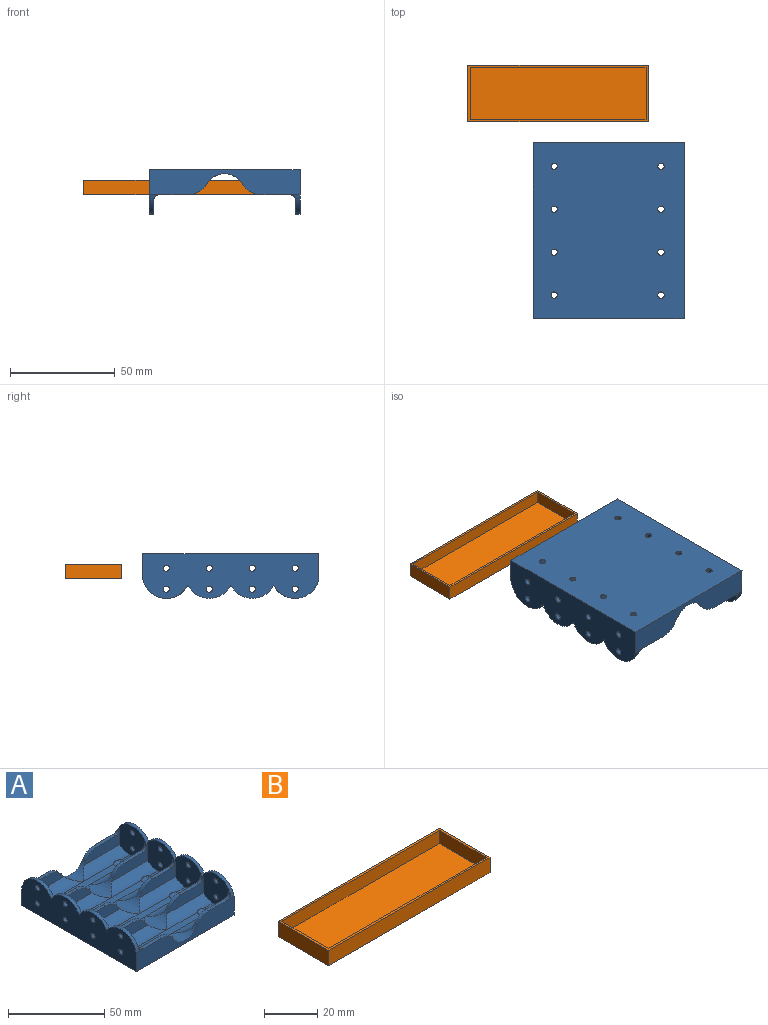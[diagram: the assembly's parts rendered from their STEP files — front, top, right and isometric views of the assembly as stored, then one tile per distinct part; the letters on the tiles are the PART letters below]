
ASSEMBLY  parts=2 mates=1
PART A: 158 faces, bbox 72x84x21.4 mm
  f0: plane 84x21.43mm, normal (-1,0,0), area 1579.3mm2, adj f1,f144,f145,f146,f147,f148,f149,f150
  f1: cylinder r=1.5mm len=3mm, axis (-1,0,0), area 18.8mm2, adj f0,f2
  f2: plane 82.05x19.43mm, normal (1,0,0), area 1230.6mm2, adj f1,f3,f120,f121,f122,f123,f124,f125
  f3: cylinder r=3mm len=3mm, axis (0,-1,0), area 7.1mm2, adj f2,f4,f120,f152
  f4: plane 13.68x2mm, normal (0,0,1), area 27.4mm2, adj f3,f5,f120,f151
  f5: cylinder r=10mm len=8.66mm, axis (0,-1,0), area 20.9mm2, adj f4,f6,f120,f151
  f6: cylinder r=10mm len=17.32mm, axis (0,-1,0), area 98.7mm2, adj f5,f7,f118,f119,f120,f121,f151
  f7: cylinder r=10mm len=34mm, axis (-1,0,0), area 237.5mm2, adj f6,f8,f114,f116,f117,f118
  f8: plane 45.41x4.22mm, normal (0,0,1), area 187.5mm2, adj f7,f9,f15,f19,f121,f123
  f9: cone r=1.5mm half-angle=45deg, axis (0,0,1), area 9.1mm2, adj f8,f10,f13,f157
  f10: bspline ~5.59x2.36mm, area 12.3mm2, adj f9,f11,f12,f123
  f11: cylinder r=1.5mm len=2.39mm, axis (0,0,1), area 0mm2, adj f10,f157
  f12: cone r=1.5mm half-angle=45deg, axis (0,0,1), area 9.1mm2, adj f10,f13,f122,f157
  f13: bspline ~5.59x2.36mm, area 12.3mm2, adj f9,f12,f14,f121
  f14: cylinder r=1.5mm len=2.39mm, axis (0,0,1), area 0mm2, adj f13,f157
  f15: cone r=1.5mm half-angle=45deg, axis (0,0,1), area 9.1mm2, adj f8,f16,f114,f157
  f16: bspline ~5.59x2.36mm, area 12.3mm2, adj f15,f17,f18,f19
  f17: cylinder r=1.5mm len=2.39mm, axis (0,0,1), area 0mm2, adj f16,f157
  f18: cone r=1.5mm half-angle=45deg, axis (0,0,1), area 9.1mm2, adj f16,f114,f116,f157
  f19: cylinder r=10mm len=34mm, axis (-1,0,0), area 237.5mm2, adj f8,f16,f20,f113,f116,f117
  f20: cylinder r=10mm len=17.32mm, axis (0,-1,0), area 155.5mm2, adj f19,f21,f23,f109,f112,f113,f123,f124
  f21: cylinder r=10mm len=8.66mm, axis (0,-1,0), area 20.9mm2, adj f20,f22,f124,f126
  f22: plane 13.68x2mm, normal (0,0,1), area 27.4mm2, adj f21,f124,f125,f126
  f23: cylinder r=10mm len=34mm, axis (-1,0,0), area 237.5mm2, adj f20,f24,f106,f108,f109,f117
  f24: plane 45.41x4.22mm, normal (0,0,1), area 187.5mm2, adj f23,f25,f29,f100,f127,f129
  f25: cone r=1.5mm half-angle=45deg, axis (0,0,1), area 9.1mm2, adj f24,f26,f106,f157
  f26: bspline ~5.59x2.36mm, area 12.3mm2, adj f25,f27,f28,f29
  f27: cone r=1.5mm half-angle=45deg, axis (0,0,1), area 9.1mm2, adj f26,f106,f108,f157
  f28: cylinder r=1.5mm len=2.39mm, axis (0,0,1), area 0mm2, adj f26,f157
  f29: cylinder r=10mm len=34mm, axis (-1,0,0), area 237.5mm2, adj f24,f26,f30,f97,f108,f117
  f30: plane 26.86x10mm, normal (0,1,0), area 168.1mm2, adj f29,f31,f95,f96,f97,f117
  f31: cylinder r=10mm len=8.66mm, axis (0,1,0), area 20.9mm2, adj f30,f32,f96,f97
  f32: plane 26.86x10mm, normal (0,-1,0), area 168.1mm2, adj f31,f33,f95,f96,f97,f117
  f33: cylinder r=10mm len=34mm, axis (-1,0,0), area 237.5mm2, adj f32,f34,f92,f94,f97,f117
  f34: plane 45.41x4.22mm, normal (0,0,1), area 187.5mm2, adj f33,f35,f41,f45,f133,f135
  f35: cone r=1.5mm half-angle=45deg, axis (0,0,1), area 9.1mm2, adj f34,f36,f39,f157
  f36: bspline ~5.59x2.36mm, area 12.3mm2, adj f35,f37,f38,f135
  f37: cylinder r=1.5mm len=2.39mm, axis (0,0,1), area 0mm2, adj f36,f157
  f38: cone r=1.5mm half-angle=45deg, axis (0,0,1), area 9.1mm2, adj f36,f39,f134,f157
  f39: bspline ~5.59x2.36mm, area 12.3mm2, adj f35,f38,f40,f133
  f40: cylinder r=1.5mm len=2.39mm, axis (0,0,1), area 0mm2, adj f39,f157
  f41: cone r=1.5mm half-angle=45deg, axis (0,0,1), area 9.1mm2, adj f34,f42,f92,f157
  f42: bspline ~5.59x2.36mm, area 12.3mm2, adj f41,f43,f44,f45
  f43: cylinder r=1.5mm len=2.39mm, axis (0,0,1), area 0mm2, adj f42,f157
  f44: cone r=1.5mm half-angle=45deg, axis (0,0,1), area 9.1mm2, adj f42,f92,f94,f157
  f45: cylinder r=10mm len=34mm, axis (-1,0,0), area 237.5mm2, adj f34,f42,f46,f91,f94,f117
  f46: cylinder r=10mm len=17.32mm, axis (0,1,0), area 155.5mm2, adj f45,f47,f49,f87,f90,f91,f135,f136
  f47: cylinder r=10mm len=8.66mm, axis (0,1,0), area 20.9mm2, adj f46,f48,f136,f138
  f48: plane 13.68x2mm, normal (0,0,1), area 27.4mm2, adj f47,f136,f137,f138
  f49: cylinder r=10mm len=34mm, axis (-1,0,0), area 237.5mm2, adj f46,f50,f84,f86,f87,f117
  f50: plane 45.41x4.22mm, normal (0,0,1), area 187.5mm2, adj f49,f51,f55,f78,f139,f141
  f51: cone r=1.5mm half-angle=45deg, axis (0,0,1), area 9.1mm2, adj f50,f52,f84,f157
  f52: bspline ~5.59x2.36mm, area 12.3mm2, adj f51,f53,f54,f55
  f53: cone r=1.5mm half-angle=45deg, axis (0,0,1), area 9.1mm2, adj f52,f84,f86,f157
  f54: cylinder r=1.5mm len=2.39mm, axis (0,0,1), area 0mm2, adj f52,f157
  f55: cylinder r=10mm len=34mm, axis (-1,0,0), area 237.5mm2, adj f50,f52,f56,f75,f86,f117
  f56: plane 26.86x10mm, normal (0,1,0), area 168.1mm2, adj f55,f57,f73,f74,f75,f117
  f57: cylinder r=3mm len=3mm, axis (0,-1,0), area 7.1mm2, adj f56,f58,f73,f117
  f58: cylinder r=11.43mm len=21.5mm, axis (1,0,0), area 62.1mm2, adj f57,f59,f72,f117,f156
  f59: plane 84x21.43mm, normal (1,0,0), area 1579.3mm2, adj f58,f60,f61,f62,f63,f64,f65,f66
  f60: cylinder r=1.5mm len=3mm, axis (-1,0,0), area 18.8mm2, adj f59,f117
  f61: cylinder r=1.5mm len=3mm, axis (-1,0,0), area 18.8mm2, adj f59,f117
  f62: cylinder r=1.5mm len=3mm, axis (-1,0,0), area 18.8mm2, adj f59,f117
  f63: cylinder r=1.5mm len=3mm, axis (-1,0,0), area 18.8mm2, adj f59,f117
  f64: cylinder r=1.5mm len=3mm, axis (-1,0,0), area 18.8mm2, adj f59,f117
  f65: cylinder r=1.5mm len=3mm, axis (-1,0,0), area 18.8mm2, adj f59,f117
  f66: cylinder r=1.5mm len=3mm, axis (-1,0,0), area 18.8mm2, adj f59,f117
  f67: cylinder r=1.5mm len=3mm, axis (-1,0,0), area 18.8mm2, adj f59,f117
  f68: cylinder r=11.43mm len=20.5mm, axis (1,0,0), area 50.9mm2, adj f59,f69,f72,f117
  f69: cylinder r=11.43mm len=21.5mm, axis (1,0,0), area 62.1mm2, adj f59,f68,f70,f117,f151
  f70: cylinder r=3mm len=3mm, axis (0,1,0), area 7.1mm2, adj f69,f71,f117,f118
  f71: plane 13.68x2mm, normal (0,0,1), area 27.4mm2, adj f70,f118,f119,f151
  f72: cylinder r=11.43mm len=20.5mm, axis (1,0,0), area 50.9mm2, adj f58,f59,f68,f117
  f73: plane 13.68x2mm, normal (0,0,1), area 27.4mm2, adj f56,f57,f74,f156
  f74: cylinder r=10mm len=8.66mm, axis (0,1,0), area 20.9mm2, adj f56,f73,f75,f156
  f75: cylinder r=10mm len=17.32mm, axis (0,1,0), area 98.7mm2, adj f55,f56,f74,f76,f141,f142,f156
  f76: cylinder r=10mm len=8.66mm, axis (0,1,0), area 20.9mm2, adj f75,f77,f142,f156
  f77: plane 13.68x2mm, normal (0,0,1), area 27.4mm2, adj f76,f142,f143,f156
  f78: cone r=1.5mm half-angle=45deg, axis (0,0,1), area 9.1mm2, adj f50,f79,f82,f157
  f79: bspline ~5.59x2.36mm, area 12.3mm2, adj f78,f80,f81,f139
  f80: cone r=1.5mm half-angle=45deg, axis (0,0,1), area 9.1mm2, adj f79,f82,f140,f157
  f81: cylinder r=1.5mm len=2.39mm, axis (0,0,1), area 0mm2, adj f79,f157
  f82: bspline ~5.59x2.36mm, area 12.3mm2, adj f78,f80,f83,f141
  f83: cylinder r=1.5mm len=2.39mm, axis (0,0,1), area 0mm2, adj f82,f157
  f84: bspline ~5.59x2.36mm, area 12.3mm2, adj f49,f51,f53,f85
  f85: cylinder r=1.5mm len=2.39mm, axis (0,0,1), area 0mm2, adj f84,f157
  f86: plane 6.21x4.22mm, normal (0,0,1), area 24.1mm2, adj f49,f53,f55,f117
  f87: plane 26.86x10mm, normal (0,-1,0), area 168.1mm2, adj f46,f49,f88,f89,f90,f117
  f88: cylinder r=3mm len=3mm, axis (0,-1,0), area 9.4mm2, adj f87,f89,f91,f117
  f89: plane 13.68x2mm, normal (0,0,1), area 27.4mm2, adj f87,f88,f90,f91
  f90: cylinder r=10mm len=8.66mm, axis (0,1,0), area 20.9mm2, adj f46,f87,f89,f91
  f91: plane 26.86x10mm, normal (0,1,0), area 168.1mm2, adj f45,f46,f88,f89,f90,f117
  f92: bspline ~5.59x2.36mm, area 12.3mm2, adj f33,f41,f44,f93
  f93: cylinder r=1.5mm len=2.39mm, axis (0,0,1), area 0mm2, adj f92,f157
  f94: plane 6.21x4.22mm, normal (0,0,1), area 24.1mm2, adj f33,f44,f45,f117
  f95: cylinder r=3mm len=3mm, axis (0,-1,0), area 9.4mm2, adj f30,f32,f96,f117
  f96: plane 13.68x2mm, normal (0,0,1), area 27.4mm2, adj f30,f31,f32,f95
  f97: cylinder r=10mm len=17.32mm, axis (0,1,0), area 155.5mm2, adj f29,f30,f31,f32,f33,f98,f129,f130
  f98: cylinder r=10mm len=8.66mm, axis (0,1,0), area 20.9mm2, adj f97,f99,f130,f132
  f99: plane 13.68x2mm, normal (0,0,1), area 27.4mm2, adj f98,f130,f131,f132
  f100: cone r=1.5mm half-angle=45deg, axis (0,0,1), area 9.1mm2, adj f24,f101,f104,f157
  f101: bspline ~5.59x2.36mm, area 12.3mm2, adj f100,f102,f103,f127
  f102: cone r=1.5mm half-angle=45deg, axis (0,0,1), area 9.1mm2, adj f101,f104,f128,f157
  f103: cylinder r=1.5mm len=2.39mm, axis (0,0,1), area 0mm2, adj f101,f157
  f104: bspline ~5.59x2.36mm, area 12.3mm2, adj f100,f102,f105,f129
  f105: cylinder r=1.5mm len=2.39mm, axis (0,0,1), area 0mm2, adj f104,f157
  f106: bspline ~5.59x2.36mm, area 12.3mm2, adj f23,f25,f27,f107
  f107: cylinder r=1.5mm len=2.39mm, axis (0,0,1), area 0mm2, adj f106,f157
  f108: plane 6.21x4.22mm, normal (0,0,1), area 24.1mm2, adj f23,f27,f29,f117
  f109: plane 26.86x10mm, normal (0,-1,0), area 168.1mm2, adj f20,f23,f110,f111,f112,f117
  f110: plane 13.68x2mm, normal (0,0,1), area 27.4mm2, adj f109,f111,f112,f113
  f111: cylinder r=3mm len=3mm, axis (0,1,0), area 9.4mm2, adj f109,f110,f113,f117
  f112: cylinder r=10mm len=8.66mm, axis (0,-1,0), area 20.9mm2, adj f20,f109,f110,f113
  f113: plane 26.86x10mm, normal (0,1,0), area 168.1mm2, adj f19,f20,f110,f111,f112,f117
  f114: bspline ~5.59x2.36mm, area 12.3mm2, adj f7,f15,f18,f115
  f115: cylinder r=1.5mm len=2.39mm, axis (0,0,1), area 0mm2, adj f114,f157
  f116: plane 6.21x4.22mm, normal (0,0,1), area 24.1mm2, adj f7,f18,f19,f117
  f117: plane 82.05x19.43mm, normal (-1,0,0), area 1230.6mm2, adj f7,f19,f23,f29,f30,f32,f33,f45
  f118: plane 26.86x10mm, normal (0,-1,0), area 168.1mm2, adj f6,f7,f70,f71,f117,f119
  f119: cylinder r=10mm len=8.66mm, axis (0,-1,0), area 20.9mm2, adj f6,f71,f118,f151
  f120: plane 26.86x10mm, normal (0,-1,0), area 168.1mm2, adj f2,f3,f4,f5,f6,f121
  f121: cylinder r=10mm len=34mm, axis (-1,0,0), area 237.5mm2, adj f2,f6,f8,f13,f120,f122
  f122: plane 5.21x4.22mm, normal (0,0,1), area 19.9mm2, adj f2,f12,f121,f123
  f123: cylinder r=10mm len=34mm, axis (-1,0,0), area 237.5mm2, adj f2,f8,f10,f20,f122,f124
  f124: plane 26.86x10mm, normal (0,1,0), area 168.1mm2, adj f2,f20,f21,f22,f123,f125
  f125: cylinder r=3mm len=3mm, axis (0,-1,0), area 9.4mm2, adj f2,f22,f124,f126
  f126: plane 26.86x10mm, normal (0,-1,0), area 168.1mm2, adj f2,f20,f21,f22,f125,f127
  f127: cylinder r=10mm len=34mm, axis (-1,0,0), area 237.5mm2, adj f2,f20,f24,f101,f126,f128
  f128: plane 5.21x4.22mm, normal (0,0,1), area 19.9mm2, adj f2,f102,f127,f129
  f129: cylinder r=10mm len=34mm, axis (-1,0,0), area 237.5mm2, adj f2,f24,f97,f104,f128,f130
  f130: plane 26.86x10mm, normal (0,1,0), area 168.1mm2, adj f2,f97,f98,f99,f129,f131
  f131: cylinder r=3mm len=3mm, axis (0,1,0), area 9.4mm2, adj f2,f99,f130,f132
  f132: plane 26.86x10mm, normal (0,-1,0), area 168.1mm2, adj f2,f97,f98,f99,f131,f133
  f133: cylinder r=10mm len=34mm, axis (-1,0,0), area 237.5mm2, adj f2,f34,f39,f97,f132,f134
  f134: plane 5.21x4.22mm, normal (0,0,1), area 19.9mm2, adj f2,f38,f133,f135
  f135: cylinder r=10mm len=34mm, axis (-1,0,0), area 237.5mm2, adj f2,f34,f36,f46,f134,f136
  f136: plane 26.86x10mm, normal (0,1,0), area 168.1mm2, adj f2,f46,f47,f48,f135,f137
  f137: cylinder r=3mm len=3mm, axis (0,1,0), area 9.4mm2, adj f2,f48,f136,f138
  f138: plane 26.86x10mm, normal (0,-1,0), area 168.1mm2, adj f2,f46,f47,f48,f137,f139
  f139: cylinder r=10mm len=34mm, axis (-1,0,0), area 237.5mm2, adj f2,f46,f50,f79,f138,f140
  f140: plane 5.21x4.22mm, normal (0,0,1), area 19.9mm2, adj f2,f80,f139,f141
  f141: cylinder r=10mm len=34mm, axis (-1,0,0), area 237.5mm2, adj f2,f50,f75,f82,f140,f142
  f142: plane 26.86x10mm, normal (0,1,0), area 168.1mm2, adj f2,f75,f76,f77,f141,f143
  f143: cylinder r=3mm len=3mm, axis (0,1,0), area 7.1mm2, adj f2,f77,f142,f155
  f144: cylinder r=1.5mm len=3mm, axis (-1,0,0), area 18.8mm2, adj f0,f2
  f145: cylinder r=1.5mm len=3mm, axis (-1,0,0), area 18.8mm2, adj f0,f2
  f146: cylinder r=1.5mm len=3mm, axis (-1,0,0), area 18.8mm2, adj f0,f2
  f147: cylinder r=1.5mm len=3mm, axis (-1,0,0), area 18.8mm2, adj f0,f2
  f148: cylinder r=1.5mm len=3mm, axis (-1,0,0), area 18.8mm2, adj f0,f2
  f149: cylinder r=1.5mm len=3mm, axis (-1,0,0), area 18.8mm2, adj f0,f2
  f150: cylinder r=1.5mm len=3mm, axis (-1,0,0), area 18.8mm2, adj f0,f2
  f151: plane 72x12mm, normal (0,1,0), area 690.8mm2, adj f0,f4,f5,f6,f59,f69,f71,f119
  f152: cylinder r=11.43mm len=21.5mm, axis (1,0,0), area 62.1mm2, adj f0,f2,f3,f151,f153
  f153: cylinder r=11.43mm len=20.5mm, axis (1,0,0), area 50.9mm2, adj f0,f2,f152,f154
  f154: cylinder r=11.43mm len=20.5mm, axis (1,0,0), area 50.9mm2, adj f0,f2,f153,f155
  f155: cylinder r=11.43mm len=21.5mm, axis (1,0,0), area 62.1mm2, adj f0,f2,f143,f154,f156
  f156: plane 72x12mm, normal (0,-1,0), area 690.8mm2, adj f0,f58,f59,f73,f74,f75,f76,f77
  f157: plane 84x72mm, normal (0,0,-1), area 5991.5mm2, adj f0,f9,f11,f12,f14,f15,f17,f18
PART B: 11 faces, bbox 86x27x7 mm
  f0: plane 86x27mm, normal (0,0,1), area 222mm2, adj f1,f2,f3,f4,f6,f7,f8,f9
  f1: plane 27x7mm, normal (-1,0,0), area 189mm2, adj f0,f2,f4,f5
  f2: plane 86x7mm, normal (0,-1,0), area 602mm2, adj f0,f1,f3,f5
  f3: plane 27x7mm, normal (1,0,0), area 189mm2, adj f0,f2,f4,f5
  f4: plane 86x7mm, normal (0,1,0), area 602mm2, adj f0,f1,f3,f5
  f5: plane 86x27mm, normal (0,0,-1), area 2322mm2, adj f1,f2,f3,f4
  f6: plane 25x6mm, normal (1,0,0), area 150mm2, adj f0,f7,f9,f10
  f7: plane 84x6mm, normal (0,1,0), area 504mm2, adj f0,f6,f8,f10
  f8: plane 25x6mm, normal (-1,0,0), area 150mm2, adj f0,f7,f9,f10
  f9: plane 84x6mm, normal (0,-1,0), area 504mm2, adj f0,f6,f8,f10
  f10: plane 84x25mm, normal (0,0,1), area 2100mm2, adj f6,f7,f8,f9
PLACE A rot(axis=(-1,0,0),180deg) t=(-28.84,-147.1,8.26)mm
PLACE B rot(axis=(0.54,0.7,-0.48),0deg) t=(-66.79,-49.92,-3.74)mm
MATE slider A.f156 <-> B.f2  axis (0,1,0) through (-53,-74.35,-3.74)mm
